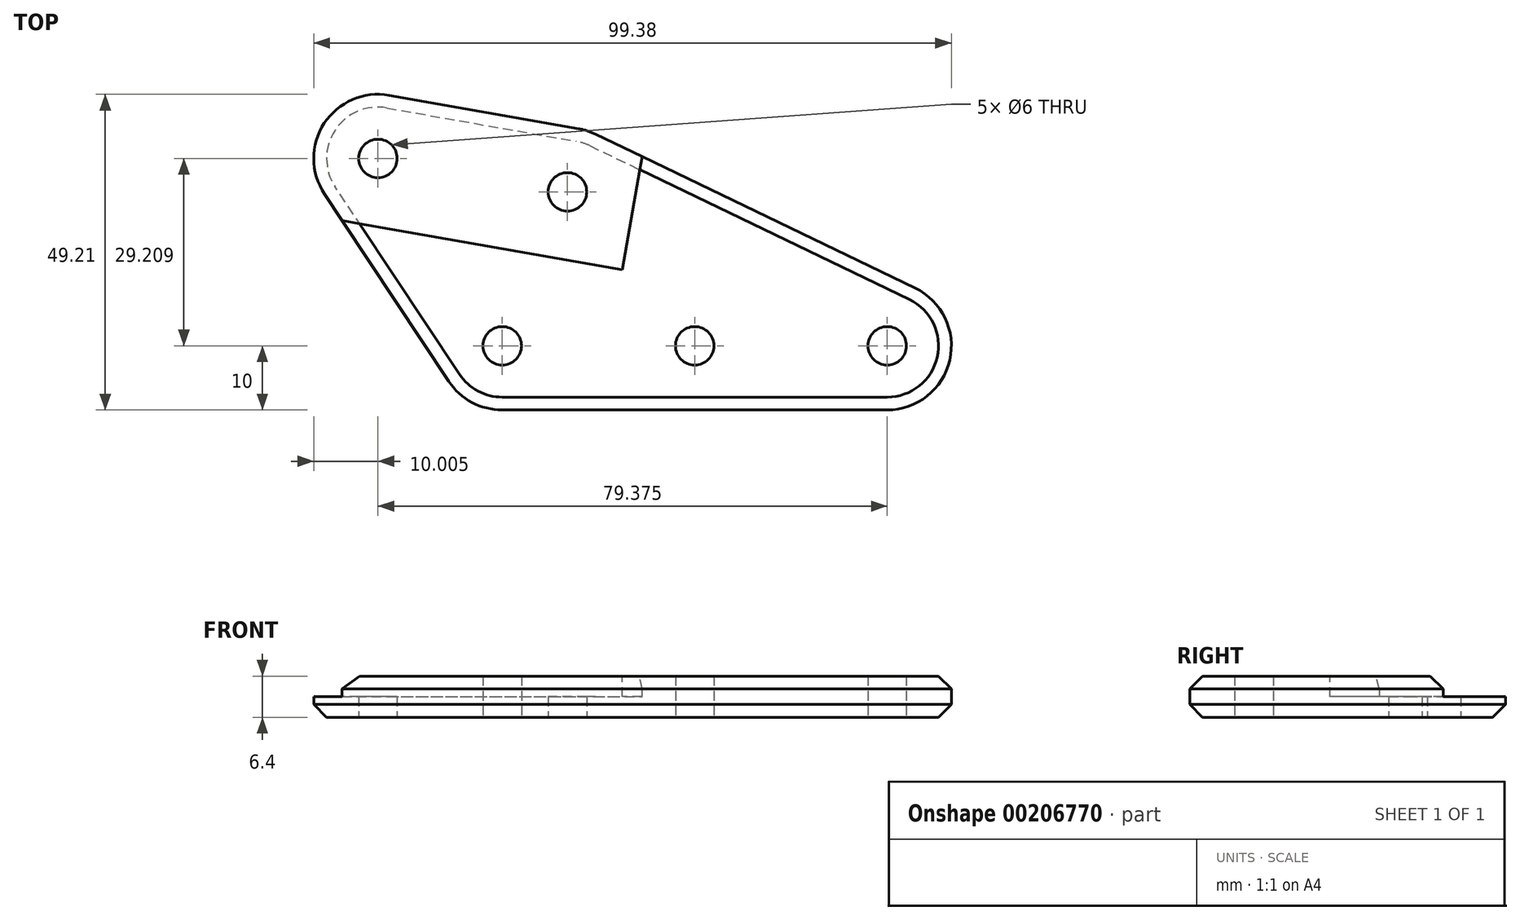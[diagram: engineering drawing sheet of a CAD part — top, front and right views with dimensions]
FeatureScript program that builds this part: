
annotation { "Feature Type Name" : "Feature", "Feature Type Description" : "" }
export const myFeature = defineFeature(function(context is Context, id is Id, definition is map)
    precondition{}
    {
        {
            var Q0;
            Q0=qCreatedBy(makeId("Top.planeOp"),FACE);
            var sketch = newSketch(context, id + "F0", { "sketchPlane" : qUnion([Q0])});
            skLineSegment(sketch, "E0", {"start": v(-30, -10) * mm, "end": v(-90, -10) * mm});
            skCircle(sketch, "E1", {"center": v(-90, 0) * mm, "radius": 3 * mm});
            skCircle(sketch, "E2", {"center": v(-109.38, 29.2) * mm, "radius": 3 * mm});
            skCircle(sketch, "E3", {"center": v(-79.83, 24) * mm, "radius": 3 * mm});
            skLineSegment(sketch, "E4", {"start": v(-90, 0) * mm, "end": v(-60, 0) * mm});
            skLineSegment(sketch, "E5", {"start": v(-30, 0) * mm, "end": v(0, 0) * mm});
            skLineSegment(sketch, "E6", {"start": v(-60, 0) * mm, "end": v(-30, 0) * mm});
            skLineSegment(sketch, "E7", {"start": v(-109.38, 29.2) * mm, "end": v(-79.83, 24) * mm});
            skCircle(sketch, "E8", {"center": v(-109.38, 29.2) * mm, "radius": 10 * mm});
            skCircle(sketch, "E9", {"center": v(-90, 0) * mm, "radius": 10 * mm});
            skCircle(sketch, "E10", {"center": v(-79.83, 24) * mm, "radius": 10 * mm});
            skLineSegment(sketch, "E11", {"start": v(-107.64, 39.06) * mm, "end": v(-78.1, 33.85) * mm});
            skPoint(sketch, "E12.startSnap0", {"position": v(-45, 0) * mm});
            skPoint(sketch, "E13.newPointB", {"position": v(1.6, -3374380.4) * mm});
            skLineSegment(sketch, "E14", {"start": v(-75.5, 33) * mm, "end": v(-25.66, 9) * mm});
            skLineSegment(sketch, "E15", {"start": v(-79.83, 24) * mm, "end": v(56.28, 0) * mm});
            skLineSegment(sketch, "E16", {"start": v(0, 0) * mm, "end": v(56.28, 0) * mm});
            skCircle(sketch, "E17", {"center": v(-60, 0) * mm, "radius": 3 * mm});
            skCircle(sketch, "E18", {"center": v(-30, 0) * mm, "radius": 3 * mm});
            skCircle(sketch, "E19", {"center": v(-30, 0) * mm, "radius": 10 * mm});
            skLineSegment(sketch, "E20", {"start": v(-117.7, 23.68) * mm, "end": v(-98.33, -5.53) * mm});
            skLineSegment(sketch, "E21.bottom", {"start": v(-102, 0) * mm, "end": v(-134.42, 0) * mm});
            skLineSegment(sketch, "E21.top", {"start": v(-102, -10) * mm, "end": v(-134.42, -10) * mm});
            skLineSegment(sketch, "E21.left", {"start": v(-102, 0) * mm, "end": v(-102, -10) * mm});
            skLineSegment(sketch, "E21.right", {"start": v(-134.42, 0) * mm, "end": v(-134.42, -10) * mm});
            skSolve(sketch);
        }
        {
            var Q0;
            {var subQ0=sQuery(id+"F0.wireOp",EDGE,"E14");var subQ1=sQuery(id+"F0.wireOp",EDGE,"E10");var subQ2=makeQuery(id+"F0.imprint","INTERSECT",VERTEX,{"derivedFrom":[subQ1,subQ0]});Q0=makeQuery(id+"F0.imprint","IMPRINT",FACE,{"disambiguationData":[TD([[makeQuery(id+"F0.imprint","IMPRINT",EDGE,{"disambiguationData":[TD([[subQ2,1.0]])],"derivedFrom":subQ1}),-1.0]])]});}
            var Q1;
            {var subQ6=sQuery(id+"F0.wireOp",EDGE,"E0");Q1=makeQuery(id+"F0.imprint","IMPRINT",FACE,{"disambiguationData":[TD([[makeQuery(id+"F0.imprint","IMPRINT",EDGE,{"derivedFrom":subQ6}),-1.0]])]});}
            var Q2;
            {var subQ5=sQuery(id+"F0.wireOp",EDGE,"E11");Q2=makeQuery(id+"F0.imprint","IMPRINT",FACE,{"disambiguationData":[TD([[makeQuery(id+"F0.imprint","IMPRINT",EDGE,{"derivedFrom":subQ5}),-1.0]])]});}
            var Q3;
            {var subQ5=sQuery(id+"F0.wireOp",EDGE,"E11");Q3=makeQuery(id+"F0.imprint","IMPRINT",FACE,{"disambiguationData":[TD([[makeQuery(id+"F0.imprint","IMPRINT",EDGE,{"derivedFrom":subQ5}),-1.0]])]});}
            var Q4;
            {var subQ0=sQuery(id+"F0.wireOp",EDGE,"E7");var subQ1=sQuery(id+"F0.wireOp",EDGE,"E3");var subQ2=makeQuery(id+"F0.imprint","INTERSECT",VERTEX,{"derivedFrom":[subQ1,subQ0]});Q4=makeQuery(id+"F0.imprint","IMPRINT",FACE,{"disambiguationData":[TD([[makeQuery(id+"F0.imprint","IMPRINT",EDGE,{"disambiguationData":[TD([[subQ2,-1.0]])],"derivedFrom":subQ1}),-1.0]])]});}
            var Q5;
            {var subQ0=sQuery(id+"F0.wireOp",EDGE,"E14");var subQ1=sQuery(id+"F0.wireOp",EDGE,"E10");var subQ2=makeQuery(id+"F0.imprint","INTERSECT",VERTEX,{"derivedFrom":[subQ1,subQ0]});Q5=makeQuery(id+"F0.imprint","IMPRINT",FACE,{"disambiguationData":[TD([[makeQuery(id+"F0.imprint","IMPRINT",EDGE,{"disambiguationData":[TD([[subQ2,1.0]])],"derivedFrom":subQ1}),-1.0]])]});}
            var Q6;
            {var subQ2=sQuery(id+"F0.wireOp",EDGE,"E7");var subQ5=sQuery(id+"F0.wireOp",EDGE,"E3");var subQ9=makeQuery(id+"F0.imprint","INTERSECT",VERTEX,{"derivedFrom":[subQ5,subQ2]});Q6=makeQuery(id+"F0.imprint","IMPRINT",FACE,{"disambiguationData":[TD([[makeQuery(id+"F0.imprint","IMPRINT",EDGE,{"disambiguationData":[TD([[subQ9,1.0]])],"derivedFrom":subQ5}),-1.0]])]});}
            var Q7;
            {var subQ1=sQuery(id+"F0.wireOp",EDGE,"E4");var subQ16=sQuery(id+"F0.wireOp",EDGE,"E9");var subQ18=makeQuery(id+"F0.imprint","INTERSECT",VERTEX,{"derivedFrom":[subQ1,subQ16]});Q7=makeQuery(id+"F0.imprint","IMPRINT",FACE,{"disambiguationData":[TD([[makeQuery(id+"F0.imprint","IMPRINT",EDGE,{"disambiguationData":[TD([[subQ18,-1.0]])],"derivedFrom":subQ1}),1.0]])]});}
            var Q8;
            {var subQ6=sQuery(id+"F0.wireOp",EDGE,"E0");Q8=makeQuery(id+"F0.imprint","IMPRINT",FACE,{"disambiguationData":[TD([[makeQuery(id+"F0.imprint","IMPRINT",EDGE,{"derivedFrom":subQ6}),-1.0]])]});}
            var Q9;
            Q9=makeQuery(id+"F0.imprint","IMPRINT",FACE,{"disambiguationData":[TD([[makeQuery(id+"F0.imprint","IMPRINT",EDGE,{"derivedFrom":sQuery(id+"F0.wireOp",EDGE,"E1")}),-1.0]])]});
            var Q10;
            Q10=makeQuery(id+"F0.imprint","IMPRINT",FACE,{"disambiguationData":[TD([[makeQuery(id+"F0.imprint","IMPRINT",EDGE,{"derivedFrom":sQuery(id+"F0.wireOp",EDGE,"E2")}),-1.0]])]});
            var Q11;
            {var subQ1=sQuery(id+"F0.wireOp",EDGE,"E5");var subQ5=sQuery(id+"F0.wireOp",EDGE,"E19");var subQ8=makeQuery(id+"F0.imprint","INTERSECT",VERTEX,{"derivedFrom":[subQ1,subQ5]});Q11=makeQuery(id+"F0.imprint","IMPRINT",FACE,{"disambiguationData":[TD([[makeQuery(id+"F0.imprint","IMPRINT",EDGE,{"disambiguationData":[TD([[subQ8,1.0]])],"derivedFrom":subQ1}),-1.0]])]});}
            var Q12;
            {var subQ0=sQuery(id+"F0.wireOp",EDGE,"E19");var subQ2=sQuery(id+"F0.wireOp",EDGE,"E5");var subQ3=makeQuery(id+"F0.imprint","INTERSECT",VERTEX,{"derivedFrom":[subQ2,subQ0]});Q12=makeQuery(id+"F0.imprint","IMPRINT",FACE,{"disambiguationData":[TD([[makeQuery(id+"F0.imprint","IMPRINT",EDGE,{"disambiguationData":[TD([[subQ3,1.0]])],"derivedFrom":subQ2}),1.0]])]});}
            extrude(context, id + "F1", {"entities" : qUnion([Q0, Q1, Q2, Q3, Q4, Q5, Q6, Q7, Q8, Q9, Q10, Q11, Q12]), "depth" : 6.4 * mm});
        }
        {
            var Q0;
            Q0=makeQuery(id+"F1.opExtrude","CAP_FACE",FACE,{"disambiguationData":[OSD([sQuery(id+"F0.wireOp",EDGE,"E0"),sQuery(id+"F0.wireOp",EDGE,"6dyDcM5c-1yAg-quQ1-icmL-2Ec9erfbZDdK"),sQuery(id+"F0.wireOp",EDGE,"E1"),sQuery(id+"F0.wireOp",EDGE,"E2"),sQuery(id+"F0.wireOp",EDGE,"E3"),sQuery(id+"F0.wireOp",EDGE,"E8"),sQuery(id+"F0.wireOp",EDGE,"E9"),sQuery(id+"F0.wireOp",EDGE,"MG3xochi-pTH6-NXDe-IZer-cky7eGSUGF28"),sQuery(id+"F0.wireOp",EDGE,"E10"),sQuery(id+"F0.wireOp",EDGE,"4jy32K5d-2140-3yTE-HOG5-iwpzrp11MGxu"),sQuery(id+"F0.wireOp",EDGE,"E11"),sQuery(id+"F0.wireOp",EDGE,"E14"),sQuery(id+"F0.wireOp",EDGE,"KXRvfklZ-nFMY-xIWL-Wxfe-Wy6mN7gEAxao"),sQuery(id+"F0.wireOp",EDGE,"E17"),sQuery(id+"F0.wireOp",EDGE,"E18")])],"isStart":false});
            cPlane(context, id + "F2", {"entities" : qUnion([Q0]), "cplaneType" : CPlaneType.OFFSET, "offset" : 0 * mm, "width" : 150 * mm, "height" : 150 * mm});
        }
        {
            var Q0;
            Q0=qCreatedBy(id+"F2.planeOp",FACE);
            var sketch = newSketch(context, id + "F3", { "sketchPlane" : qUnion([Q0])});
            skLineSegment(sketch, "E22", {"start": v(-125.64, 21.41) * mm, "end": v(-71.31, 11.84) * mm});
            skCircle(sketch, "E23", {"center": v(-109.38, 29.2) * mm, "radius": 10.5 * mm});
            skCircle(sketch, "E24", {"center": v(-79.83, 24) * mm, "radius": 10.5 * mm});
            skLineSegment(sketch, "E25", {"start": v(-125.64, 21.41) * mm, "end": v(-121.52, 44.76) * mm});
            skLineSegment(sketch, "E26", {"start": v(-121.52, 44.76) * mm, "end": v(-67.2, 35.18) * mm});
            skLineSegment(sketch, "E27", {"start": v(-67.2, 35.18) * mm, "end": v(-71.31, 11.84) * mm});
            skSolve(sketch);
        }
        {
            var Q0;
            Q0=qSketchRegion(id+"F3",true);
            extrude(context, id + "F4", {"entities" : qUnion([Q0]), "operationType" : NewBodyOperationType.REMOVE, "oppositeDirection" : true, "depth" : 3.2 * mm});
        }
        {
            var Q0;
            Q0=makeQuery(id+"F1.opExtrude","CAP_EDGE",EDGE,{"disambiguationData":[OSD([sQuery(id+"F0.wireOp",EDGE,"E14")])],"isStart":true});
            var Q1;
            Q1=makeQuery(id+"F1.opExtrude","CAP_EDGE",EDGE,{"disambiguationData":[OSD([sQuery(id+"F0.wireOp",EDGE,"E14")])],"isStart":false});
            chamfer(context, id + "F5", {"entities" : qUnion([Q0, Q1]), "width" : 2 * mm, "tangentPropagation" : true});
        }
        {
            var Q0;
            Q0=makeQuery(id+"F1.opExtrude","SWEPT_BODY",BODY,{"disambiguationData":[OSD([sQuery(id+"F0.wireOp",EDGE,"E0"),sQuery(id+"F0.wireOp",EDGE,"E1"),sQuery(id+"F0.wireOp",EDGE,"E2"),sQuery(id+"F0.wireOp",EDGE,"E3"),sQuery(id+"F0.wireOp",EDGE,"E8"),sQuery(id+"F0.wireOp",EDGE,"E9"),sQuery(id+"F0.wireOp",EDGE,"E10"),sQuery(id+"F0.wireOp",EDGE,"E11"),sQuery(id+"F0.wireOp",EDGE,"E14"),sQuery(id+"F0.wireOp",EDGE,"E17"),sQuery(id+"F0.wireOp",EDGE,"E18"),sQuery(id+"F0.wireOp",EDGE,"E19"),sQuery(id+"F0.wireOp",EDGE,"E20")])]});
            var Q1;
            Q1=makeQuery(id+"F1.opExtrude","CAP_FACE",FACE,{"disambiguationData":[OSD([sQuery(id+"F0.wireOp",EDGE,"E0"),sQuery(id+"F0.wireOp",EDGE,"E1"),sQuery(id+"F0.wireOp",EDGE,"E2"),sQuery(id+"F0.wireOp",EDGE,"E3"),sQuery(id+"F0.wireOp",EDGE,"E8"),sQuery(id+"F0.wireOp",EDGE,"E9"),sQuery(id+"F0.wireOp",EDGE,"E10"),sQuery(id+"F0.wireOp",EDGE,"E11"),sQuery(id+"F0.wireOp",EDGE,"E14"),sQuery(id+"F0.wireOp",EDGE,"E17"),sQuery(id+"F0.wireOp",EDGE,"E18"),sQuery(id+"F0.wireOp",EDGE,"E19"),sQuery(id+"F0.wireOp",EDGE,"E20")])],"isStart":false});
            mirror(context, id + "F6", {"entities" : qUnion([Q0]), "mirrorPlane" : qUnion([Q1])});
        }
        {
            var Q0;
            Q0=makeQuery(id+"F1.opExtrude","SWEPT_BODY",BODY,{"disambiguationData":[OSD([sQuery(id+"F0.wireOp",EDGE,"E0"),sQuery(id+"F0.wireOp",EDGE,"E1"),sQuery(id+"F0.wireOp",EDGE,"E2"),sQuery(id+"F0.wireOp",EDGE,"E3"),sQuery(id+"F0.wireOp",EDGE,"E8"),sQuery(id+"F0.wireOp",EDGE,"E9"),sQuery(id+"F0.wireOp",EDGE,"E10"),sQuery(id+"F0.wireOp",EDGE,"E11"),sQuery(id+"F0.wireOp",EDGE,"E14"),sQuery(id+"F0.wireOp",EDGE,"E17"),sQuery(id+"F0.wireOp",EDGE,"E18"),sQuery(id+"F0.wireOp",EDGE,"E19"),sQuery(id+"F0.wireOp",EDGE,"E20")])]});
            deleteBodies(context, id + "F7", {"entities" : qUnion([Q0])});
        }
        {
            var Q0;
            Q0=makeQuery(id+"F6.opPattern","COPY",BODY,{"derivedFrom":makeQuery(id+"F1.opExtrude","SWEPT_BODY",BODY,{"disambiguationData":[OSD([sQuery(id+"F0.wireOp",EDGE,"E0"),sQuery(id+"F0.wireOp",EDGE,"E1"),sQuery(id+"F0.wireOp",EDGE,"E2"),sQuery(id+"F0.wireOp",EDGE,"E3"),sQuery(id+"F0.wireOp",EDGE,"E8"),sQuery(id+"F0.wireOp",EDGE,"E9"),sQuery(id+"F0.wireOp",EDGE,"E10"),sQuery(id+"F0.wireOp",EDGE,"E11"),sQuery(id+"F0.wireOp",EDGE,"E14"),sQuery(id+"F0.wireOp",EDGE,"E17"),sQuery(id+"F0.wireOp",EDGE,"E18"),sQuery(id+"F0.wireOp",EDGE,"E19"),sQuery(id+"F0.wireOp",EDGE,"E20")])]}),"instanceName":"1"});
            var Q1;
            Q1=makeQuery(id+"F6.opPattern","COPY",FACE,{"derivedFrom":makeQuery(id+"F1.opExtrude","CAP_FACE",FACE,{"disambiguationData":[OSD([sQuery(id+"F0.wireOp",EDGE,"E0"),sQuery(id+"F0.wireOp",EDGE,"E1"),sQuery(id+"F0.wireOp",EDGE,"E2"),sQuery(id+"F0.wireOp",EDGE,"E3"),sQuery(id+"F0.wireOp",EDGE,"E8"),sQuery(id+"F0.wireOp",EDGE,"E9"),sQuery(id+"F0.wireOp",EDGE,"E10"),sQuery(id+"F0.wireOp",EDGE,"E11"),sQuery(id+"F0.wireOp",EDGE,"E14"),sQuery(id+"F0.wireOp",EDGE,"E17"),sQuery(id+"F0.wireOp",EDGE,"E18"),sQuery(id+"F0.wireOp",EDGE,"E19"),sQuery(id+"F0.wireOp",EDGE,"E20")])],"isStart":true}),"instanceName":"1"});
            mirror(context, id + "F8", {"entities" : qUnion([Q0]), "mirrorPlane" : qUnion([Q1])});
        }
        {
            var Q0;
            Q0=makeQuery(id+"F6.opPattern","COPY",BODY,{"derivedFrom":makeQuery(id+"F1.opExtrude","SWEPT_BODY",BODY,{"disambiguationData":[OSD([sQuery(id+"F0.wireOp",EDGE,"E0"),sQuery(id+"F0.wireOp",EDGE,"E1"),sQuery(id+"F0.wireOp",EDGE,"E2"),sQuery(id+"F0.wireOp",EDGE,"E3"),sQuery(id+"F0.wireOp",EDGE,"E8"),sQuery(id+"F0.wireOp",EDGE,"E9"),sQuery(id+"F0.wireOp",EDGE,"E10"),sQuery(id+"F0.wireOp",EDGE,"E11"),sQuery(id+"F0.wireOp",EDGE,"E14"),sQuery(id+"F0.wireOp",EDGE,"E17"),sQuery(id+"F0.wireOp",EDGE,"E18"),sQuery(id+"F0.wireOp",EDGE,"E19"),sQuery(id+"F0.wireOp",EDGE,"E20")])]}),"instanceName":"1"});
            deleteBodies(context, id + "F9", {"entities" : qUnion([Q0])});
        }
    });
